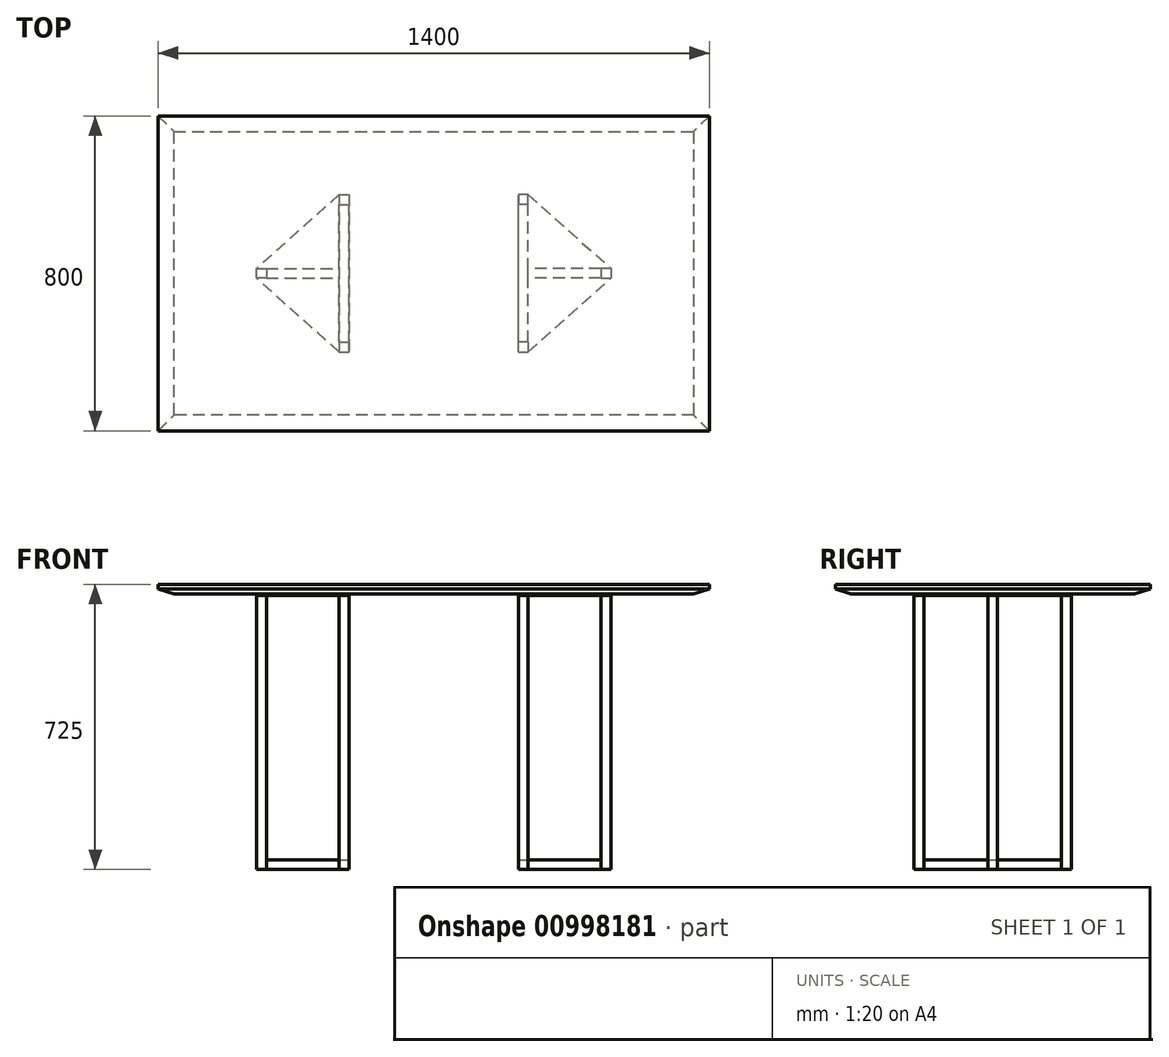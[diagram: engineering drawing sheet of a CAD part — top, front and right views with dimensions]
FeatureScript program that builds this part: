
annotation { "Feature Type Name" : "Feature", "Feature Type Description" : "" }
export const myFeature = defineFeature(function(context is Context, id is Id, definition is map)
    precondition{}
    {
        {
            var Q0;
            Q0=qCreatedBy(makeId("Top.planeOp"),FACE);
            var sketch = newSketch(context, id + "F0", { "sketchPlane" : qUnion([Q0])});
            skLineSegment(sketch, "E0.bottom", {"start": v(0, 0) * mm, "end": v(-1400, 0) * mm, "construction": true});
            skLineSegment(sketch, "E0.top", {"start": v(0, 800) * mm, "end": v(-1400, 800) * mm, "construction": true});
            skLineSegment(sketch, "E0.left", {"start": v(0, 0) * mm, "end": v(0, 800) * mm, "construction": true});
            skLineSegment(sketch, "E0.right", {"start": v(-1400, 0) * mm, "end": v(-1400, 800) * mm, "construction": true});
            skLineSegment(sketch, "E1", {"start": v(-700, 0) * mm, "end": v(-700, 800) * mm, "construction": true});
            skLineSegment(sketch, "E2", {"start": v(-1400, 400) * mm, "end": v(0, 400) * mm, "construction": true});
            skLineSegment(sketch, "E3", {"start": v(0, 400) * mm, "end": v(-250, 400) * mm, "construction": true});
            skLineSegment(sketch, "E4", {"start": v(0, 400) * mm, "end": v(-460, 400) * mm, "construction": true});
            skLineSegment(sketch, "E5", {"start": v(-460, 400) * mm, "end": v(-460, 800) * mm, "construction": true});
            skLineSegment(sketch, "E6", {"start": v(-460, 800) * mm, "end": v(-460, 600) * mm, "construction": true});
            skLineSegment(sketch, "E7", {"start": v(-460, 600) * mm, "end": v(-485, 600) * mm});
            skLineSegment(sketch, "E8", {"start": v(-485, 600) * mm, "end": v(-485, 575) * mm});
            skLineSegment(sketch, "E9", {"start": v(-485, 575) * mm, "end": v(-460, 575) * mm});
            skLineSegment(sketch, "E10", {"start": v(-460, 575) * mm, "end": v(-460, 600) * mm});
            skLineSegment(sketch, "E11", {"start": v(-250, 400) * mm, "end": v(-250, 412.5) * mm});
            skLineSegment(sketch, "E12", {"start": v(-250, 412.5) * mm, "end": v(-275, 412.5) * mm});
            skLineSegment(sketch, "E13", {"start": v(-275, 412.5) * mm, "end": v(-275, 387.5) * mm});
            skLineSegment(sketch, "E14", {"start": v(-275, 387.5) * mm, "end": v(-250, 387.5) * mm});
            skLineSegment(sketch, "E15", {"start": v(-250, 387.5) * mm, "end": v(-250, 412.5) * mm});
            skLineSegment(sketch, "E16.MirrorCS", {"start": v(-460, 200) * mm, "end": v(-485, 200) * mm});
            skLineSegment(sketch, "E17.MirrorCS", {"start": v(-485, 225) * mm, "end": v(-460, 225) * mm});
            skLineSegment(sketch, "E18.MirrorCS", {"start": v(-485, 200) * mm, "end": v(-485, 225) * mm});
            skLineSegment(sketch, "E19.MirrorCS", {"start": v(-460, 225) * mm, "end": v(-460, 200) * mm});
            skLineSegment(sketch, "E20.MirrorCS", {"start": v(-940, 600) * mm, "end": v(-915, 600) * mm});
            skLineSegment(sketch, "E21.MirrorCS", {"start": v(-915, 600) * mm, "end": v(-915, 575) * mm});
            skLineSegment(sketch, "E22.MirrorCS", {"start": v(-915, 575) * mm, "end": v(-940, 575) * mm});
            skLineSegment(sketch, "E23.MirrorCS", {"start": v(-915, 200) * mm, "end": v(-915, 225) * mm});
            skLineSegment(sketch, "E24.MirrorCS", {"start": v(-915, 225) * mm, "end": v(-940, 225) * mm});
            skLineSegment(sketch, "E25.MirrorCS", {"start": v(-940, 200) * mm, "end": v(-915, 200) * mm});
            skLineSegment(sketch, "E26.MirrorCS", {"start": v(-940, 225) * mm, "end": v(-940, 200) * mm});
            skLineSegment(sketch, "E27.MirrorCS", {"start": v(-1150, 412.5) * mm, "end": v(-1125, 412.5) * mm});
            skLineSegment(sketch, "E28.MirrorCS", {"start": v(-1125, 412.5) * mm, "end": v(-1125, 387.5) * mm});
            skLineSegment(sketch, "E29.MirrorCS", {"start": v(-1125, 387.5) * mm, "end": v(-1150, 387.5) * mm});
            skLineSegment(sketch, "E30.MirrorCS", {"start": v(-1150, 387.5) * mm, "end": v(-1150, 412.5) * mm});
            skLineSegment(sketch, "E31", {"start": v(-940, 600) * mm, "end": v(-940, 575) * mm});
            skSolve(sketch);
        }
        {
            var Q0;
            Q0 = qSketchRegion(id + "F0", true);
            extrude(context, id + "F1", {"entities" : qUnion([Q0]), "depth" : 700 * mm, "offsetDistance" : 25 * mm});
        }
        {
            var Q0;
            Q0=makeQuery(id+"F1.opExtrude","SWEPT_FACE",FACE,{"disambiguationData":[OSD([sQuery(id+"F0.wireOp",EDGE,"E9")])]});
            cPlane(context, id + "F2", {"entities" : qUnion([Q0]), "cplaneType" : CPlaneType.OFFSET, "offset" : 0 * mm, "width" : 150 * mm, "height" : 150 * mm});
        }
        {
            var Q0;
            Q0=qCreatedBy(id+"F2.planeOp",FACE);
            var sketch = newSketch(context, id + "F3", { "sketchPlane" : qUnion([Q0])});
            skLineSegment(sketch, "E32", {"start": v(0, 0) * mm, "end": v(-460, 0) * mm});
            skLineSegment(sketch, "E33", {"start": v(-460, 0) * mm, "end": v(-485, 0) * mm});
            skLineSegment(sketch, "E34", {"start": v(-485, 0) * mm, "end": v(-485, 25) * mm});
            skLineSegment(sketch, "E35", {"start": v(-485, 25) * mm, "end": v(-460, 25) * mm});
            skLineSegment(sketch, "E36", {"start": v(-460, 25) * mm, "end": v(-460, 0) * mm});
            skSolve(sketch);
        }
        {
            var Q0;
            Q0 = qSketchRegion(id + "F3", true);
            extrude(context, id + "F4", {"entities" : qUnion([Q0]), "depth" : 350 * mm, "offsetDistance" : 25 * mm});
        }
        {
            var Q0;
            Q0=makeQuery(id+"F4.opExtrude","SWEPT_FACE",FACE,{"disambiguationData":[OSD([sQuery(id+"F3.wireOp",EDGE,"E36")])]});
            cPlane(context, id + "F5", {"entities" : qUnion([Q0]), "cplaneType" : CPlaneType.OFFSET, "offset" : 0 * mm, "width" : 150 * mm, "height" : 150 * mm});
        }
        {
            var Q0;
            Q0=qCreatedBy(id+"F5.planeOp",FACE);
            var sketch = newSketch(context, id + "F6", { "sketchPlane" : qUnion([Q0])});
            skLineSegment(sketch, "E37", {"start": v(0, 0) * mm, "end": v(387.5, 0) * mm, "construction": true});
            skLineSegment(sketch, "E38", {"start": v(387.5, 0) * mm, "end": v(412.5, 0) * mm});
            skLineSegment(sketch, "E39", {"start": v(412.5, 0) * mm, "end": v(412.5, 25) * mm});
            skLineSegment(sketch, "E40", {"start": v(412.5, 25) * mm, "end": v(387.5, 25) * mm});
            skLineSegment(sketch, "E41", {"start": v(387.5, 25) * mm, "end": v(387.5, 0) * mm});
            skSolve(sketch);
        }
        {
            var Q0;
            Q0 = qSketchRegion(id + "F6", true);
            extrude(context, id + "F7", {"entities" : qUnion([Q0]), "depth" : 185 * mm, "offsetDistance" : 25 * mm});
        }
        {
            var Q0;
            Q0=makeQuery(id+"F1.opExtrude","SWEPT_FACE",FACE,{"disambiguationData":[OSD([sQuery(id+"F0.wireOp",EDGE,"E22.MirrorCS")])]});
            cPlane(context, id + "F8", {"entities" : qUnion([Q0]), "cplaneType" : CPlaneType.OFFSET, "offset" : 0 * mm, "width" : 150 * mm, "height" : 150 * mm});
        }
        {
            var Q0;
            Q0=qCreatedBy(id+"F8.planeOp",FACE);
            var sketch = newSketch(context, id + "F9", { "sketchPlane" : qUnion([Q0])});
            skLineSegment(sketch, "E42", {"start": v(0, 0) * mm, "end": v(-700, 0) * mm, "construction": true});
            skLineSegment(sketch, "E43", {"start": v(-700, 0) * mm, "end": v(-915, 0) * mm, "construction": true});
            skLineSegment(sketch, "E44", {"start": v(-915, 0) * mm, "end": v(-940, 0) * mm});
            skLineSegment(sketch, "E45", {"start": v(-940, 0) * mm, "end": v(-940, 25) * mm});
            skLineSegment(sketch, "E46", {"start": v(-940, 25) * mm, "end": v(-915, 25) * mm});
            skLineSegment(sketch, "E47", {"start": v(-915, 25) * mm, "end": v(-915, 0) * mm});
            skSolve(sketch);
        }
        {
            var Q0;
            Q0 = qSketchRegion(id + "F9", true);
            extrude(context, id + "F10", {"entities" : qUnion([Q0]), "operationType" : NewBodyOperationType.ADD, "depth" : 350 * mm, "offsetDistance" : 25 * mm});
        }
        {
            var Q0;
            Q0=makeQuery(id+"F10.boolean.opBoolean","MERGE",FACE,{"derivedFrom":[makeQuery(id+"F1.opExtrude","SWEPT_FACE",FACE,{"disambiguationData":[OSD([sQuery(id+"F0.wireOp",EDGE,"E31")])]}),makeQuery(id+"F10.opExtrude","SWEPT_FACE",FACE,{"disambiguationData":[OSD([sQuery(id+"F9.wireOp",EDGE,"E45")])]})]});
            cPlane(context, id + "F11", {"entities" : qUnion([Q0]), "cplaneType" : CPlaneType.OFFSET, "offset" : 0 * mm, "width" : 150 * mm, "height" : 150 * mm});
        }
        {
            var Q0;
            Q0=qCreatedBy(id+"F11.planeOp",FACE);
            var sketch = newSketch(context, id + "F12", { "sketchPlane" : qUnion([Q0])});
            skLineSegment(sketch, "E48", {"start": v(0, 0) * mm, "end": v(-387.5, 0) * mm, "construction": true});
            skLineSegment(sketch, "E49", {"start": v(-387.5, 0) * mm, "end": v(-387.5, 25) * mm});
            skLineSegment(sketch, "E50", {"start": v(-387.5, 25) * mm, "end": v(-412.5, 25) * mm});
            skLineSegment(sketch, "E51", {"start": v(-412.5, 25) * mm, "end": v(-412.5, 0) * mm});
            skLineSegment(sketch, "E52", {"start": v(-412.5, 0) * mm, "end": v(-387.5, 0) * mm});
            skSolve(sketch);
        }
        {
            var Q0;
            Q0 = qSketchRegion(id + "F12", true);
            extrude(context, id + "F13", {"entities" : qUnion([Q0]), "depth" : 185 * mm, "offsetDistance" : 25 * mm});
        }
        {
            var Q0;
            Q0=makeQuery(id+"F1.opExtrude","CAP_FACE",FACE,{"disambiguationData":[OSD([sQuery(id+"F0.wireOp",EDGE,"E7"),sQuery(id+"F0.wireOp",EDGE,"E8"),sQuery(id+"F0.wireOp",EDGE,"E9"),sQuery(id+"F0.wireOp",EDGE,"E10")])],"isStart":false});
            cPlane(context, id + "F14", {"entities" : qUnion([Q0]), "cplaneType" : CPlaneType.OFFSET, "offset" : 0 * mm, "width" : 150 * mm, "height" : 150 * mm});
        }
        {
            var Q0;
            Q0=qCreatedBy(id+"F14.planeOp",FACE);
            var sketch = newSketch(context, id + "F15", { "sketchPlane" : qUnion([Q0])});
            skLineSegment(sketch, "E53.bottom", {"start": v(0, 0) * mm, "end": v(-1400, 0) * mm, "construction": true});
            skLineSegment(sketch, "E53.top", {"start": v(0, 800) * mm, "end": v(-1400, 800) * mm, "construction": true});
            skLineSegment(sketch, "E53.left", {"start": v(0, 0) * mm, "end": v(0, 800) * mm, "construction": true});
            skLineSegment(sketch, "E53.right", {"start": v(-1400, 0) * mm, "end": v(-1400, 800) * mm, "construction": true});
            skLineSegment(sketch, "E54", {"start": v(-700, 0) * mm, "end": v(-700, 400) * mm, "construction": true});
            skLineSegment(sketch, "E55", {"start": v(0, 400) * mm, "end": v(-250, 400) * mm, "construction": true});
            skLineSegment(sketch, "E56", {"start": v(-250, 400) * mm, "end": v(-250, 412.5) * mm});
            skLineSegment(sketch, "E57", {"start": v(-700, 400) * mm, "end": v(-485, 400) * mm, "construction": true});
            skLineSegment(sketch, "E58", {"start": v(-485, 400) * mm, "end": v(-485, 600) * mm});
            skLineSegment(sketch, "E59", {"start": v(-485, 600) * mm, "end": v(-460, 600) * mm});
            skLineSegment(sketch, "E60", {"start": v(-460, 600) * mm, "end": v(-250, 412.5) * mm});
            skLineSegment(sketch, "E61.MirrorCS", {"start": v(-460, 200) * mm, "end": v(-250, 387.5) * mm});
            skLineSegment(sketch, "E62.MirrorCS", {"start": v(-250, 400) * mm, "end": v(-250, 387.5) * mm});
            skLineSegment(sketch, "E63.MirrorCS", {"start": v(-485, 200) * mm, "end": v(-460, 200) * mm});
            skLineSegment(sketch, "E64.MirrorCS", {"start": v(-485, 400) * mm, "end": v(-485, 200) * mm});
            skLineSegment(sketch, "E65.MirrorCS", {"start": v(-940, 600) * mm, "end": v(-1150, 412.5) * mm});
            skLineSegment(sketch, "E66.MirrorCS", {"start": v(-1150, 400) * mm, "end": v(-1150, 412.5) * mm});
            skLineSegment(sketch, "E67.MirrorCS", {"start": v(-1150, 400) * mm, "end": v(-1150, 387.5) * mm});
            skLineSegment(sketch, "E68.MirrorCS", {"start": v(-940, 200) * mm, "end": v(-1150, 387.5) * mm});
            skLineSegment(sketch, "E69.MirrorCS", {"start": v(-915, 400) * mm, "end": v(-915, 600) * mm});
            skLineSegment(sketch, "E70.MirrorCS", {"start": v(-915, 400) * mm, "end": v(-915, 200) * mm});
            skLineSegment(sketch, "E71.MirrorCS", {"start": v(-915, 200) * mm, "end": v(-940, 200) * mm});
            skLineSegment(sketch, "E72.MirrorCS", {"start": v(-915, 600) * mm, "end": v(-940, 600) * mm});
            skSolve(sketch);
        }
        {
            var Q0;
            Q0 = qSketchRegion(id + "F15", true);
            extrude(context, id + "F16", {"entities" : qUnion([Q0]), "oppositeDirection" : true, "depth" : 3 * mm, "offsetDistance" : 25 * mm});
        }
        {
            var Q0;
            Q0=makeQuery(id+"F16.opExtrude","CAP_FACE",FACE,{"disambiguationData":[OSD([sQuery(id+"F15.wireOp",EDGE,"E65.MirrorCS"),sQuery(id+"F15.wireOp",EDGE,"E66.MirrorCS"),sQuery(id+"F15.wireOp",EDGE,"E67.MirrorCS"),sQuery(id+"F15.wireOp",EDGE,"E68.MirrorCS"),sQuery(id+"F15.wireOp",EDGE,"E69.MirrorCS"),sQuery(id+"F15.wireOp",EDGE,"E70.MirrorCS"),sQuery(id+"F15.wireOp",EDGE,"E71.MirrorCS"),sQuery(id+"F15.wireOp",EDGE,"E72.MirrorCS")])],"isStart":true});
            cPlane(context, id + "F17", {"entities" : qUnion([Q0]), "cplaneType" : CPlaneType.OFFSET, "offset" : 0 * mm, "width" : 150 * mm, "height" : 150 * mm});
        }
        {
            var Q0;
            Q0=qCreatedBy(id+"F17.planeOp",FACE);
            var sketch = newSketch(context, id + "F18", { "sketchPlane" : qUnion([Q0])});
            skLineSegment(sketch, "E73.bottom", {"start": v(0, 0) * mm, "end": v(-1400, 0) * mm});
            skLineSegment(sketch, "E73.top", {"start": v(0, 800) * mm, "end": v(-1400, 800) * mm});
            skLineSegment(sketch, "E73.left", {"start": v(0, 0) * mm, "end": v(0, 800) * mm});
            skLineSegment(sketch, "E73.right", {"start": v(-1400, 0) * mm, "end": v(-1400, 800) * mm});
            skSolve(sketch);
        }
        {
            var Q0;
            Q0 = qSketchRegion(id + "F18", true);
            extrude(context, id + "F19", {"entities" : qUnion([Q0]), "depth" : 25 * mm, "offsetDistance" : 25 * mm});
        }
        {
            var Q0;
            Q0=makeQuery(id+"F19.opExtrude","CAP_FACE",FACE,{"disambiguationData":[OSD([sQuery(id+"F18.wireOp",EDGE,"E73.bottom"),sQuery(id+"F18.wireOp",EDGE,"E73.top"),sQuery(id+"F18.wireOp",EDGE,"E73.left"),sQuery(id+"F18.wireOp",EDGE,"E73.right")])],"isStart":true});
            chamfer(context, id + "F20", {"entities" : qUnion([Q0]), "chamferType" : ChamferType.TWO_OFFSETS, "width1" : 40 * mm, "oppositeDirection" : false, "width2" : 12.5 * mm, "tangentPropagation" : true});
        }
    });
